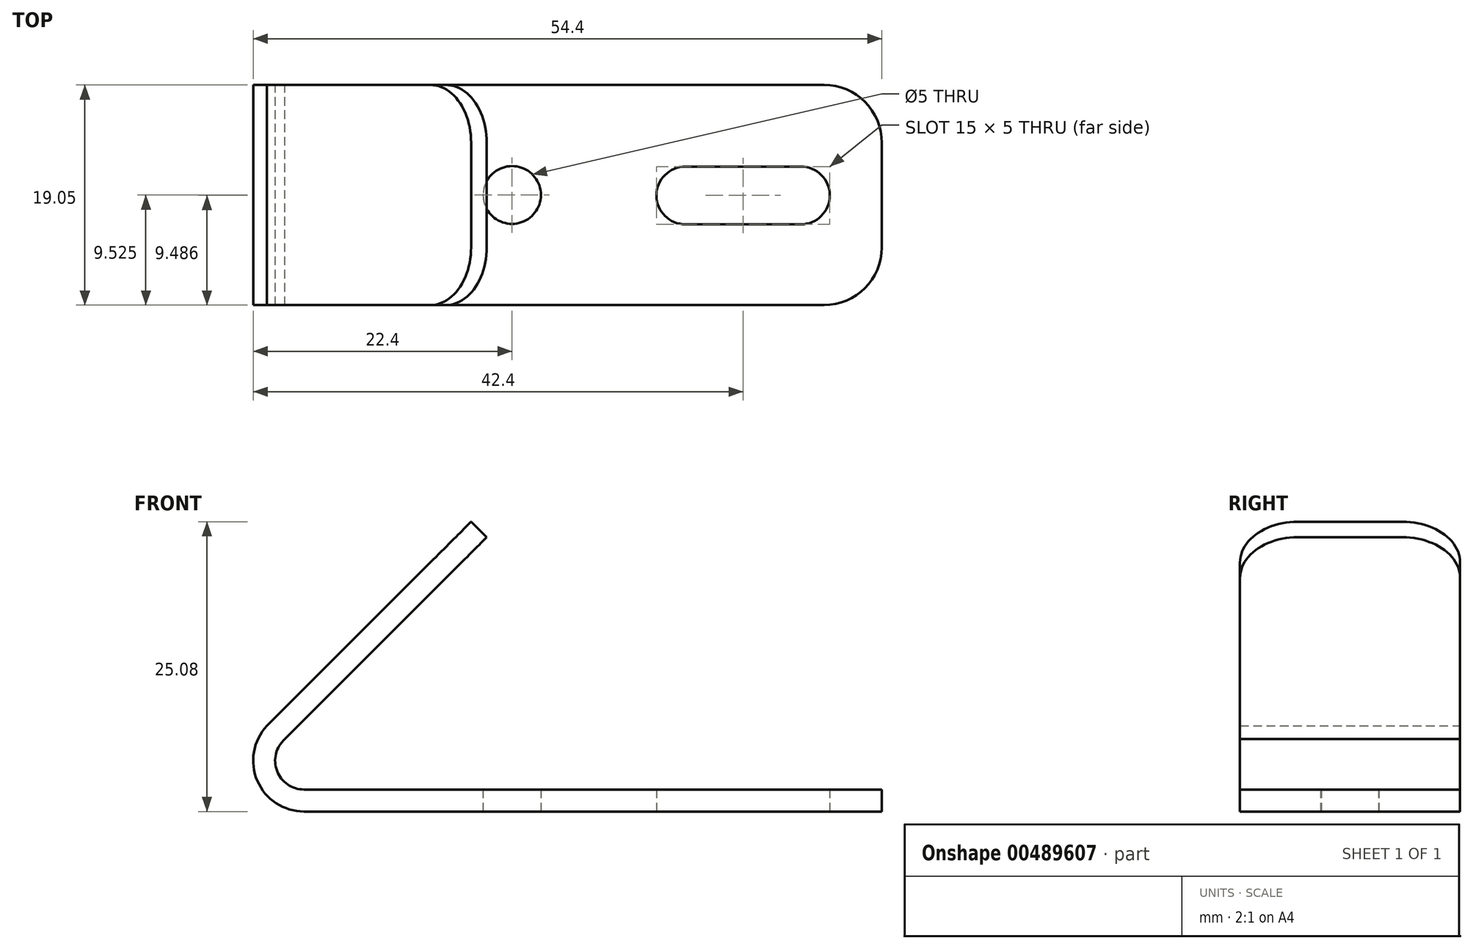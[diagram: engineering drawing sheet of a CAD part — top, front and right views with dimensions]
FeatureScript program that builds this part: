
annotation { "Feature Type Name" : "Feature", "Feature Type Description" : "" }
export const myFeature = defineFeature(function(context is Context, id is Id, definition is map)
    precondition{}
    {
        {
            var Q0;
            Q0=qCreatedBy(makeId("Front.planeOp"),FACE);
            var sketch = newSketch(context, id + "F0", { "sketchPlane" : qUnion([Q0])});
            skLineSegment(sketch, "E0.bottom", {"start": v(0, 0) * mm, "end": v(-50, 0) * mm});
            skLineSegment(sketch, "E0.top", {"start": v(0, 1.9) * mm, "end": v(-50, 1.9) * mm});
            skLineSegment(sketch, "E0.left", {"start": v(0, 0) * mm, "end": v(0, 1.9) * mm});
            skArc(sketch, "E1", {"start": v(-53, 7.62) * mm, "mid": v(-54.1, 2.79) * mm, "end": v(-50, 0) * mm});
            skArc(sketch, "E2", {"start": v(-51.66, 6.27) * mm, "mid": v(-52.34, 3.51) * mm, "end": v(-50, 1.9) * mm});
            skLineSegment(sketch, "E3", {"start": v(-51.87, 6.06) * mm, "end": v(-34.2, 23.74) * mm});
            skLineSegment(sketch, "E4", {"start": v(-53.22, 7.4) * mm, "end": v(-35.54, 25.08) * mm});
            skLineSegment(sketch, "E5", {"start": v(-35.54, 25.08) * mm, "end": v(-34.2, 23.74) * mm});
            skSolve(sketch);
        }
        {
            var Q0;
            {var subQ1=sQuery(id+"F0.wireOp",EDGE,"E0.bottom");Q0=makeQuery(id+"F0.imprint","IMPRINT",FACE,{"disambiguationData":[TD([[makeQuery(id+"F0.imprint","IMPRINT",EDGE,{"derivedFrom":subQ1}),-1.0]])]});}
            extrude(context, id + "F1", {"entities" : qUnion([Q0]), "depth" : 19.05 * mm});
        }
        {
            var Q0;
            Q0=makeQuery(id+"F1.opExtrude","CAP_EDGE",EDGE,{"disambiguationData":[OSD([sQuery(id+"F0.wireOp",EDGE,"E5")])],"isStart":true});
            var Q1;
            Q1=makeQuery(id+"F1.opExtrude","CAP_EDGE",EDGE,{"disambiguationData":[OSD([sQuery(id+"F0.wireOp",EDGE,"E5")])],"isStart":false});
            var Q2;
            Q2=makeQuery(id+"F1.opExtrude","CAP_EDGE",EDGE,{"disambiguationData":[OSD([sQuery(id+"F0.wireOp",EDGE,"E0.left")])],"isStart":true});
            var Q3;
            Q3=makeQuery(id+"F1.opExtrude","CAP_EDGE",EDGE,{"disambiguationData":[OSD([sQuery(id+"F0.wireOp",EDGE,"E0.left")])],"isStart":false});
            fillet(context, id + "F2", {"entities" : qUnion([Q0, Q1, Q2, Q3]), "radius" : 5 * mm, "tangentPropagation" : true, "allowEdgeOverflow" : false});
        }
        {
            var Q0;
            Q0=makeQuery(id+"F1.opExtrude","SWEPT_FACE",FACE,{"disambiguationData":[OSD([sQuery(id+"F0.wireOp",EDGE,"E4")])]});
            var sketch = newSketch(context, id + "F3", { "sketchPlane" : qUnion([Q0])});
            skPoint(sketch, "E6", {"position": v(-14.9, -4.5) * mm});
            skPoint(sketch, "E7", {"position": v(-14.9, -14.55) * mm});
            skCircle(sketch, "E8", {"center": v(-14.9, -4.5) * mm, "radius": 1.5 * mm});
            skCircle(sketch, "E9", {"center": v(-14.9, -14.55) * mm, "radius": 1.5 * mm});
            skSolve(sketch);
        }
        {
            var Q0;
            Q0=makeQuery(id+"F3.imprint","IMPRINT",FACE,{"disambiguationData":[TD([[makeQuery(id+"F3.imprint","IMPRINT",EDGE,{"derivedFrom":sQuery(id+"F3.wireOp",EDGE,"E8")}),1.0]])]});
            var Q1;
            Q1=makeQuery(id+"F3.imprint","IMPRINT",FACE,{"disambiguationData":[TD([[makeQuery(id+"F3.imprint","IMPRINT",EDGE,{"derivedFrom":sQuery(id+"F3.wireOp",EDGE,"E9")}),1.0]])]});
            extrude(context, id + "F4", {"entities" : qUnion([Q0, Q1]), "operationType" : NewBodyOperationType.REMOVE, "oppositeDirection" : true, "depth" : 1.9 * mm});
        }
        {
            var Q0;
            Q0=makeQuery(id+"F1.opExtrude","SWEPT_FACE",FACE,{"disambiguationData":[OSD([sQuery(id+"F0.wireOp",EDGE,"E0.bottom")])]});
            var sketch = newSketch(context, id + "F5", { "sketchPlane" : qUnion([Q0])});
            skCircle(sketch, "E10", {"center": v(-32, 9.53) * mm, "radius": 2.5 * mm});
            skLineSegment(sketch, "E11", {"start": v(-32, 9.53) * mm, "end": v(10.7, 9.53) * mm, "construction": true});
            skArc(sketch, "E12", {"start": v(-17, 12.06) * mm, "mid": v(-19.5, 9.56) * mm, "end": v(-17, 7.06) * mm});
            skArc(sketch, "E13", {"start": v(-7, 7.06) * mm, "mid": v(-4.5, 9.56) * mm, "end": v(-7, 12.06) * mm});
            skLineSegment(sketch, "E14", {"start": v(-17, 12.06) * mm, "end": v(-7, 12.06) * mm});
            skLineSegment(sketch, "E15", {"start": v(-17, 7.06) * mm, "end": v(-7, 7.06) * mm});
            skSolve(sketch);
        }
        {
            var Q0;
            Q0=makeQuery(id+"F5.imprint","IMPRINT",FACE,{"disambiguationData":[TD([[makeQuery(id+"F5.imprint","IMPRINT",EDGE,{"derivedFrom":sQuery(id+"F5.wireOp",EDGE,"E10")}),1.0]])]});
            var Q1;
            Q1=makeQuery(id+"F5.imprint","IMPRINT",FACE,{"disambiguationData":[TD([[makeQuery(id+"F5.imprint","IMPRINT",EDGE,{"derivedFrom":sQuery(id+"F5.wireOp",EDGE,"E12")}),1.0]])]});
            extrude(context, id + "F6", {"entities" : qUnion([Q0, Q1]), "operationType" : NewBodyOperationType.REMOVE, "oppositeDirection" : true, "depth" : 1.9 * mm});
        }
    });
